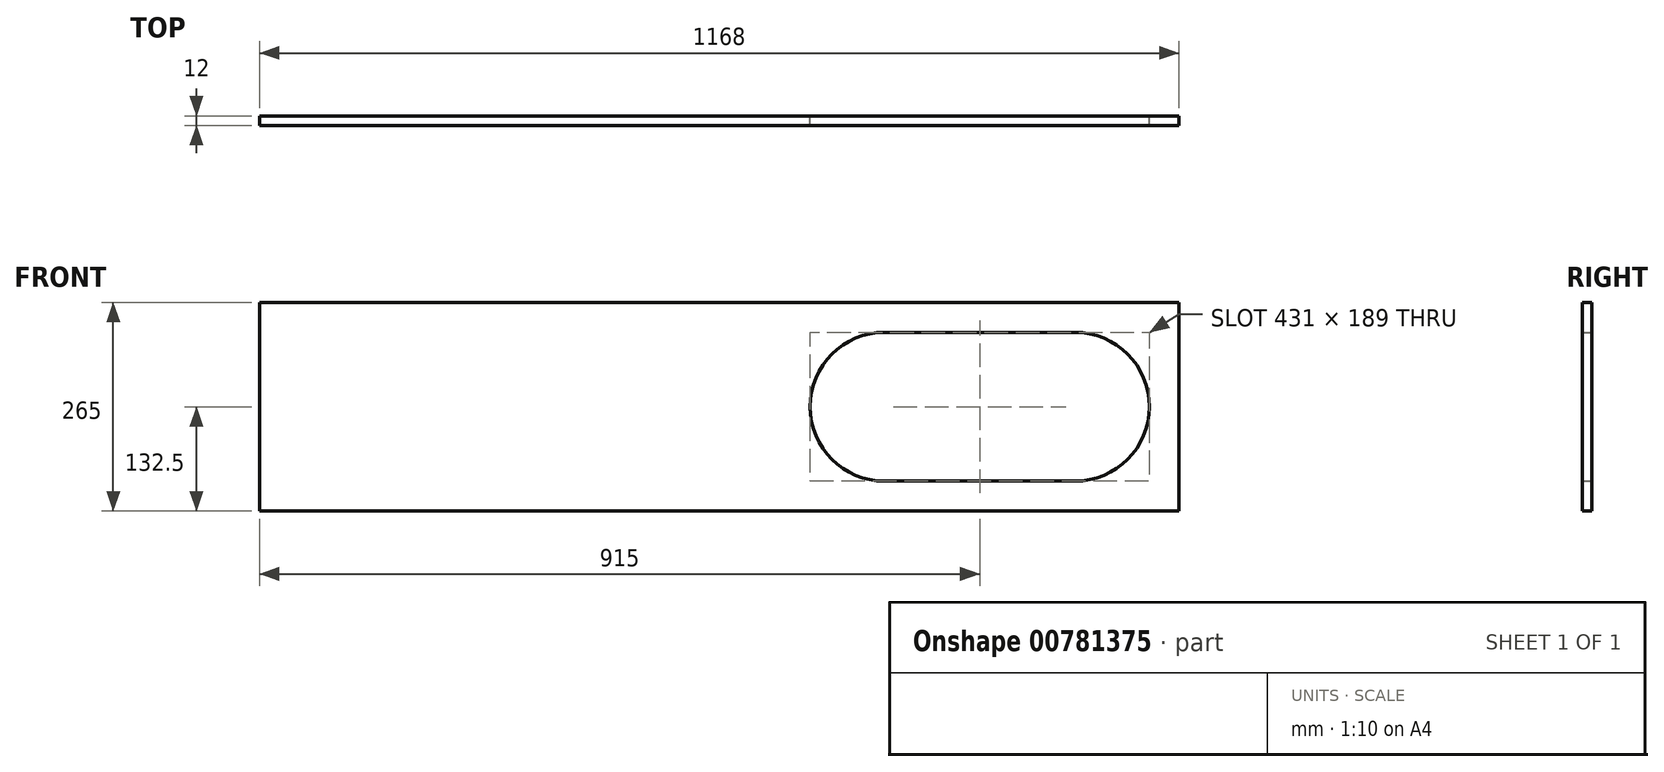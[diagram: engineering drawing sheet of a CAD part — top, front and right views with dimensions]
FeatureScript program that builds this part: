
annotation { "Feature Type Name" : "Feature", "Feature Type Description" : "" }
export const myFeature = defineFeature(function(context is Context, id is Id, definition is map)
    precondition{}
    {
        {
            var Q0;
            Q0=qCreatedBy(makeId("Front.planeOp"),FACE);
            var sketch = newSketch(context, id + "F0", { "sketchPlane" : qUnion([Q0])});
            skLineSegment(sketch, "E0.bottom", {"start": v(-584, -132.5) * mm, "end": v(584, -132.5) * mm});
            skLineSegment(sketch, "E0.top", {"start": v(-584, 132.5) * mm, "end": v(584, 132.5) * mm});
            skLineSegment(sketch, "E0.left", {"start": v(-584, -132.5) * mm, "end": v(-584, 132.5) * mm});
            skLineSegment(sketch, "E0.right", {"start": v(584, -132.5) * mm, "end": v(584, 132.5) * mm});
            skPoint(sketch, "E0.middle", {"position": v(0, 0) * mm});
            skCircle(sketch, "E1", {"center": v(452, 0) * mm, "radius": 94.5 * mm});
            skCircle(sketch, "E2", {"center": v(210, 0) * mm, "radius": 94.5 * mm});
            skCircle(sketch, "E3", {"center": v(210, 0) * mm, "radius": 111 * mm});
            skCircle(sketch, "E4", {"center": v(452, 0) * mm, "radius": 111 * mm});
            skLineSegment(sketch, "E5.bottom", {"start": v(210, 94.5) * mm, "end": v(452, 94.5) * mm});
            skLineSegment(sketch, "E5.top", {"start": v(210, -94.5) * mm, "end": v(452, -94.5) * mm});
            skLineSegment(sketch, "E5.left", {"start": v(210, 94.5) * mm, "end": v(210, -94.5) * mm});
            skLineSegment(sketch, "E5.right", {"start": v(452, 94.5) * mm, "end": v(452, -94.5) * mm});
            skSolve(sketch);
        }
        {
            var Q0;
            Q0=makeQuery(id+"F0.imprint","IMPRINT",FACE,{"disambiguationData":[TD([[makeQuery(id+"F0.imprint","IMPRINT",EDGE,{"derivedFrom":sQuery(id+"F0.wireOp",EDGE,"E0.bottom")}),1.0]])]});
            var Q1;
            {var subQ1=sQuery(id+"F0.wireOp",EDGE,"E5.bottom");var subQ6=sQuery(id+"F0.wireOp",EDGE,"E3");var subQ7=makeQuery(id+"F0.imprint","INTERSECT",VERTEX,{"derivedFrom":[subQ6,subQ1]});Q1=makeQuery(id+"F0.imprint","IMPRINT",FACE,{"disambiguationData":[TD([[makeQuery(id+"F0.imprint","IMPRINT",EDGE,{"disambiguationData":[TD([[subQ7,-1.0]])],"derivedFrom":subQ6}),1.0]])]});}
            var Q2;
            {var subQ1=sQuery(id+"F0.wireOp",EDGE,"E5.bottom");var subQ6=sQuery(id+"F0.wireOp",EDGE,"E4");var subQ7=makeQuery(id+"F0.imprint","INTERSECT",VERTEX,{"derivedFrom":[subQ6,subQ1]});Q2=makeQuery(id+"F0.imprint","IMPRINT",FACE,{"disambiguationData":[TD([[makeQuery(id+"F0.imprint","IMPRINT",EDGE,{"disambiguationData":[TD([[subQ7,1.0]])],"derivedFrom":subQ6}),1.0]])]});}
            extrude(context, id + "F1", {"entities" : qUnion([Q0, Q1, Q2]), "depth" : 12 * mm, "offsetDistance" : 25 * mm});
        }
    });
